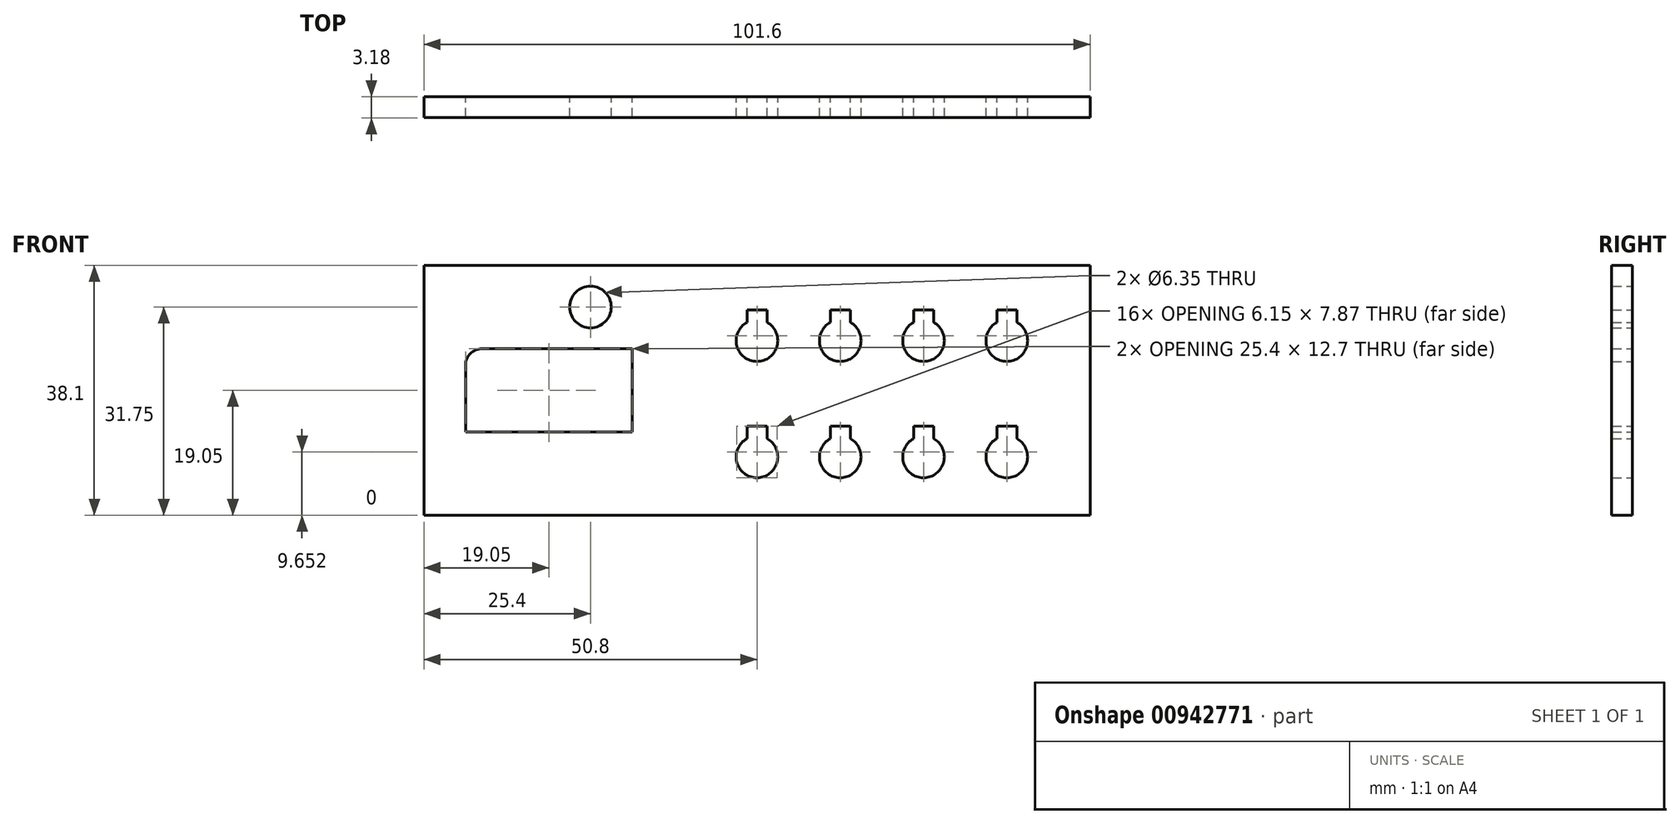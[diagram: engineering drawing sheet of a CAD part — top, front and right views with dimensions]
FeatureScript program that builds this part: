
annotation { "Feature Type Name" : "Feature", "Feature Type Description" : "" }
export const myFeature = defineFeature(function(context is Context, id is Id, definition is map)
    precondition{}
    {
        {
            var Q0;
            Q0=qCreatedBy(makeId("Front.planeOp"),FACE);
            var sketch = newSketch(context, id + "F0", { "sketchPlane" : qUnion([Q0])});
            skLineSegment(sketch, "E0.bottom", {"start": v(0, 0) * mm, "end": v(101.6, 0) * mm});
            skLineSegment(sketch, "E0.top", {"start": v(0, 38.1) * mm, "end": v(101.6, 38.1) * mm});
            skLineSegment(sketch, "E0.left", {"start": v(0, 0) * mm, "end": v(0, 38.1) * mm});
            skLineSegment(sketch, "E0.right", {"start": v(101.6, 0) * mm, "end": v(101.6, 38.1) * mm});
            skCircle(sketch, "E1", {"center": v(25.4, 31.75) * mm, "radius": 3.18 * mm});
            skArc(sketch, "E2", {"start": v(49.28, 11.68) * mm, "mid": v(50.8, 5.72) * mm, "end": v(52.32, 11.68) * mm});
            skLineSegment(sketch, "E3.bottom", {"start": v(52.32, 13.59) * mm, "end": v(49.28, 13.59) * mm});
            skLineSegment(sketch, "E3.left", {"start": v(52.32, 13.59) * mm, "end": v(52.32, 11.68) * mm});
            skLineSegment(sketch, "E3.right", {"start": v(49.28, 13.59) * mm, "end": v(49.28, 11.68) * mm});
            skPoint(sketch, "E3.middle", {"position": v(50.8, 12.07) * mm});
            skPoint(sketch, "E4.orphan", {"position": v(49.28, 10.54) * mm});
            skPoint(sketch, "E5.orphan", {"position": v(52.32, 10.54) * mm});
            skLineSegment(sketch, "E6", {"start": v(50.8, 8.9) * mm, "end": v(50.8, 12.07) * mm, "construction": true});
            skLineSegment(sketch, "E7.0.1.0", {"start": v(49.28, 31.32) * mm, "end": v(49.28, 29.4) * mm});
            skLineSegment(sketch, "E7.0.1.1", {"start": v(52.32, 31.32) * mm, "end": v(49.28, 31.32) * mm});
            skLineSegment(sketch, "E7.0.1.2", {"start": v(52.32, 31.32) * mm, "end": v(52.32, 29.4) * mm});
            skPoint(sketch, "E7.0.1.3", {"position": v(50.8, 29.8) * mm});
            skLineSegment(sketch, "E7.0.1.4", {"start": v(50.8, 26.62) * mm, "end": v(50.8, 29.8) * mm, "construction": true});
            skPoint(sketch, "E7.0.1.5", {"position": v(52.32, 28.27) * mm});
            skPoint(sketch, "E7.0.1.6", {"position": v(49.28, 28.27) * mm});
            skArc(sketch, "E7.0.1.7", {"start": v(49.28, 29.4) * mm, "mid": v(50.8, 23.44) * mm, "end": v(52.32, 29.4) * mm});
            skLineSegment(sketch, "E7.1.0.0", {"start": v(61.98, 13.59) * mm, "end": v(61.98, 11.68) * mm});
            skLineSegment(sketch, "E7.1.0.1", {"start": v(65.02, 13.59) * mm, "end": v(61.98, 13.59) * mm});
            skLineSegment(sketch, "E7.1.0.2", {"start": v(65.02, 13.59) * mm, "end": v(65.02, 11.68) * mm});
            skPoint(sketch, "E7.1.0.3", {"position": v(63.5, 12.07) * mm});
            skLineSegment(sketch, "E7.1.0.4", {"start": v(63.5, 8.9) * mm, "end": v(63.5, 12.07) * mm, "construction": true});
            skPoint(sketch, "E7.1.0.5", {"position": v(65.02, 10.54) * mm});
            skPoint(sketch, "E7.1.0.6", {"position": v(61.98, 10.54) * mm});
            skArc(sketch, "E7.1.0.7", {"start": v(61.98, 11.68) * mm, "mid": v(63.5, 5.71) * mm, "end": v(65.02, 11.68) * mm});
            skLineSegment(sketch, "E7.1.1.0", {"start": v(61.98, 31.32) * mm, "end": v(61.98, 29.4) * mm});
            skLineSegment(sketch, "E7.1.1.1", {"start": v(65.02, 31.32) * mm, "end": v(61.98, 31.32) * mm});
            skLineSegment(sketch, "E7.1.1.2", {"start": v(65.02, 31.32) * mm, "end": v(65.02, 29.4) * mm});
            skPoint(sketch, "E7.1.1.3", {"position": v(63.5, 29.8) * mm});
            skLineSegment(sketch, "E7.1.1.4", {"start": v(63.5, 26.62) * mm, "end": v(63.5, 29.8) * mm, "construction": true});
            skPoint(sketch, "E7.1.1.5", {"position": v(65.02, 28.27) * mm});
            skPoint(sketch, "E7.1.1.6", {"position": v(61.98, 28.27) * mm});
            skArc(sketch, "E7.1.1.7", {"start": v(61.98, 29.4) * mm, "mid": v(63.5, 23.44) * mm, "end": v(65.02, 29.4) * mm});
            skLineSegment(sketch, "E7.2.0.0", {"start": v(74.68, 13.59) * mm, "end": v(74.68, 11.68) * mm});
            skLineSegment(sketch, "E7.2.0.1", {"start": v(77.72, 13.59) * mm, "end": v(74.68, 13.59) * mm});
            skLineSegment(sketch, "E7.2.0.2", {"start": v(77.72, 13.59) * mm, "end": v(77.72, 11.68) * mm});
            skPoint(sketch, "E7.2.0.3", {"position": v(76.2, 12.07) * mm});
            skLineSegment(sketch, "E7.2.0.4", {"start": v(76.2, 8.9) * mm, "end": v(76.2, 12.07) * mm, "construction": true});
            skPoint(sketch, "E7.2.0.5", {"position": v(77.72, 10.54) * mm});
            skPoint(sketch, "E7.2.0.6", {"position": v(74.68, 10.54) * mm});
            skArc(sketch, "E7.2.0.7", {"start": v(74.68, 11.68) * mm, "mid": v(76.2, 5.71) * mm, "end": v(77.72, 11.68) * mm});
            skLineSegment(sketch, "E7.2.1.0", {"start": v(74.68, 31.32) * mm, "end": v(74.68, 29.4) * mm});
            skLineSegment(sketch, "E7.2.1.1", {"start": v(77.72, 31.32) * mm, "end": v(74.68, 31.32) * mm});
            skLineSegment(sketch, "E7.2.1.2", {"start": v(77.72, 31.32) * mm, "end": v(77.72, 29.4) * mm});
            skPoint(sketch, "E7.2.1.3", {"position": v(76.2, 29.8) * mm});
            skLineSegment(sketch, "E7.2.1.4", {"start": v(76.2, 26.62) * mm, "end": v(76.2, 29.8) * mm, "construction": true});
            skPoint(sketch, "E7.2.1.5", {"position": v(77.72, 28.27) * mm});
            skPoint(sketch, "E7.2.1.6", {"position": v(74.68, 28.27) * mm});
            skArc(sketch, "E7.2.1.7", {"start": v(74.68, 29.4) * mm, "mid": v(76.2, 23.44) * mm, "end": v(77.72, 29.4) * mm});
            skLineSegment(sketch, "E7.direction1", {"start": v(50.8, 8.9) * mm, "end": v(63.5, 8.9) * mm, "construction": true});
            skLineSegment(sketch, "E7.direction2", {"start": v(50.8, 8.9) * mm, "end": v(50.8, 26.62) * mm, "construction": true});
            skLineSegment(sketch, "E8.0.3.0", {"start": v(87.38, 13.59) * mm, "end": v(87.38, 11.68) * mm});
            skLineSegment(sketch, "E8.3.3.0", {"start": v(90.42, 13.59) * mm, "end": v(87.38, 13.59) * mm});
            skLineSegment(sketch, "E8.6.3.0", {"start": v(90.42, 13.59) * mm, "end": v(90.42, 11.68) * mm});
            skPoint(sketch, "E8.9.3.0", {"position": v(88.9, 12.07) * mm});
            skLineSegment(sketch, "E8.10.3.0", {"start": v(88.9, 8.9) * mm, "end": v(88.9, 12.07) * mm, "construction": true});
            skPoint(sketch, "E8.13.3.0", {"position": v(90.42, 10.54) * mm});
            skPoint(sketch, "E8.14.3.0", {"position": v(87.38, 10.54) * mm});
            skArc(sketch, "E8.15.3.0", {"start": v(87.38, 11.68) * mm, "mid": v(88.9, 5.71) * mm, "end": v(90.42, 11.68) * mm});
            skLineSegment(sketch, "E8.0.3.1", {"start": v(87.38, 31.32) * mm, "end": v(87.38, 29.4) * mm});
            skLineSegment(sketch, "E8.3.3.1", {"start": v(90.42, 31.32) * mm, "end": v(87.38, 31.32) * mm});
            skLineSegment(sketch, "E8.6.3.1", {"start": v(90.42, 31.32) * mm, "end": v(90.42, 29.4) * mm});
            skPoint(sketch, "E8.9.3.1", {"position": v(88.9, 29.8) * mm});
            skLineSegment(sketch, "E8.10.3.1", {"start": v(88.9, 26.62) * mm, "end": v(88.9, 29.8) * mm, "construction": true});
            skPoint(sketch, "E8.13.3.1", {"position": v(90.42, 28.27) * mm});
            skPoint(sketch, "E8.14.3.1", {"position": v(87.38, 28.27) * mm});
            skArc(sketch, "E8.15.3.1", {"start": v(87.38, 29.4) * mm, "mid": v(88.9, 23.44) * mm, "end": v(90.42, 29.4) * mm});
            skLineSegment(sketch, "E9.bottom", {"start": v(6.35, 12.7) * mm, "end": v(31.75, 12.7) * mm});
            skLineSegment(sketch, "E9.top", {"start": v(8.9, 25.4) * mm, "end": v(31.75, 25.4) * mm});
            skLineSegment(sketch, "E9.left", {"start": v(6.35, 12.7) * mm, "end": v(6.35, 22.86) * mm});
            skLineSegment(sketch, "E9.right", {"start": v(31.75, 12.7) * mm, "end": v(31.75, 25.4) * mm});
            skPoint(sketch, "E10.visualSharp", {"position": v(6.35, 25.4) * mm});
            skArc(sketch, "E10.filletArc", {"start": v(8.9, 25.4) * mm, "mid": v(7.1, 24.66) * mm, "end": v(6.35, 22.86) * mm});
            skSolve(sketch);
        }
        {
            var Q0;
            Q0 = qSketchRegion(id + "F0", true);
            extrude(context, id + "F1", {"entities" : qUnion([Q0]), "depth" : 3.17 * mm, "offsetDistance" : 25.4 * mm});
        }
    });
